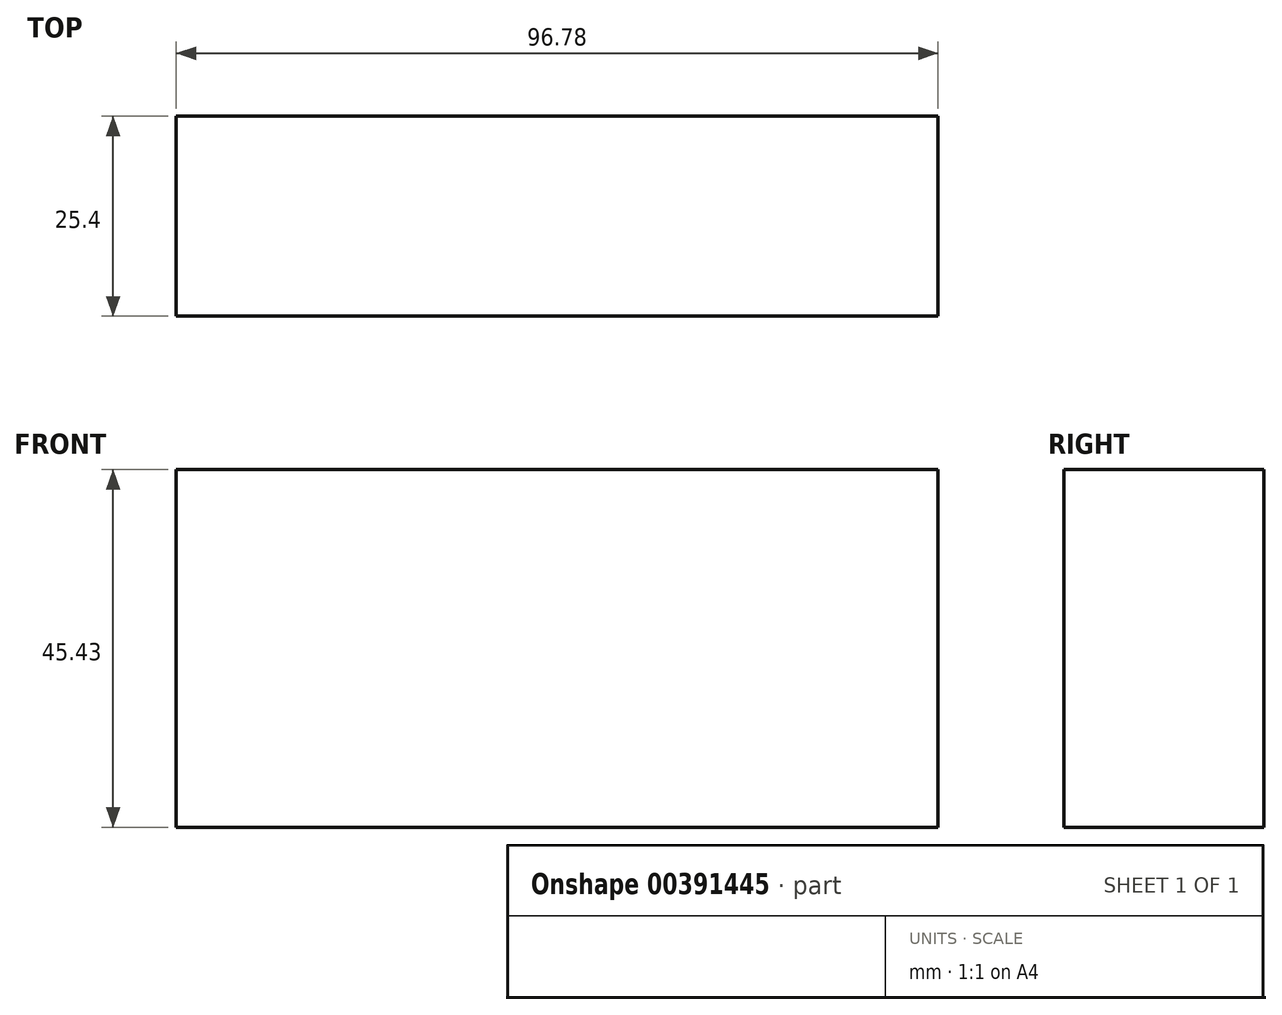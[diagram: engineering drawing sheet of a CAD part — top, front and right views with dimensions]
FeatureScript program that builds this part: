
annotation { "Feature Type Name" : "Feature", "Feature Type Description" : "" }
export const myFeature = defineFeature(function(context is Context, id is Id, definition is map)
    precondition{}
    {
        {
            var Q0;
            Q0=qCreatedBy(makeId("Front.planeOp"),FACE);
            var sketch = newSketch(context, id + "F0", { "sketchPlane" : qUnion([Q0])});
            skLineSegment(sketch, "E0.bottom", {"start": v(20.05, 0) * mm, "end": v(116.83, 0) * mm});
            skLineSegment(sketch, "E0.top", {"start": v(20.05, 45.43) * mm, "end": v(116.83, 45.43) * mm});
            skLineSegment(sketch, "E0.left", {"start": v(20.05, 0) * mm, "end": v(20.05, 45.43) * mm});
            skLineSegment(sketch, "E0.right", {"start": v(116.83, 0) * mm, "end": v(116.83, 45.43) * mm});
            skPoint(sketch, "E0.middle", {"position": v(68.44, 22.72) * mm});
            skSolve(sketch);
        }
        {
            var Q0;
            Q0 = qSketchRegion(id + "F0", true);
            extrude(context, id + "F1", {"entities" : qUnion([Q0]), "depth" : 25.4 * mm});
        }
    });
